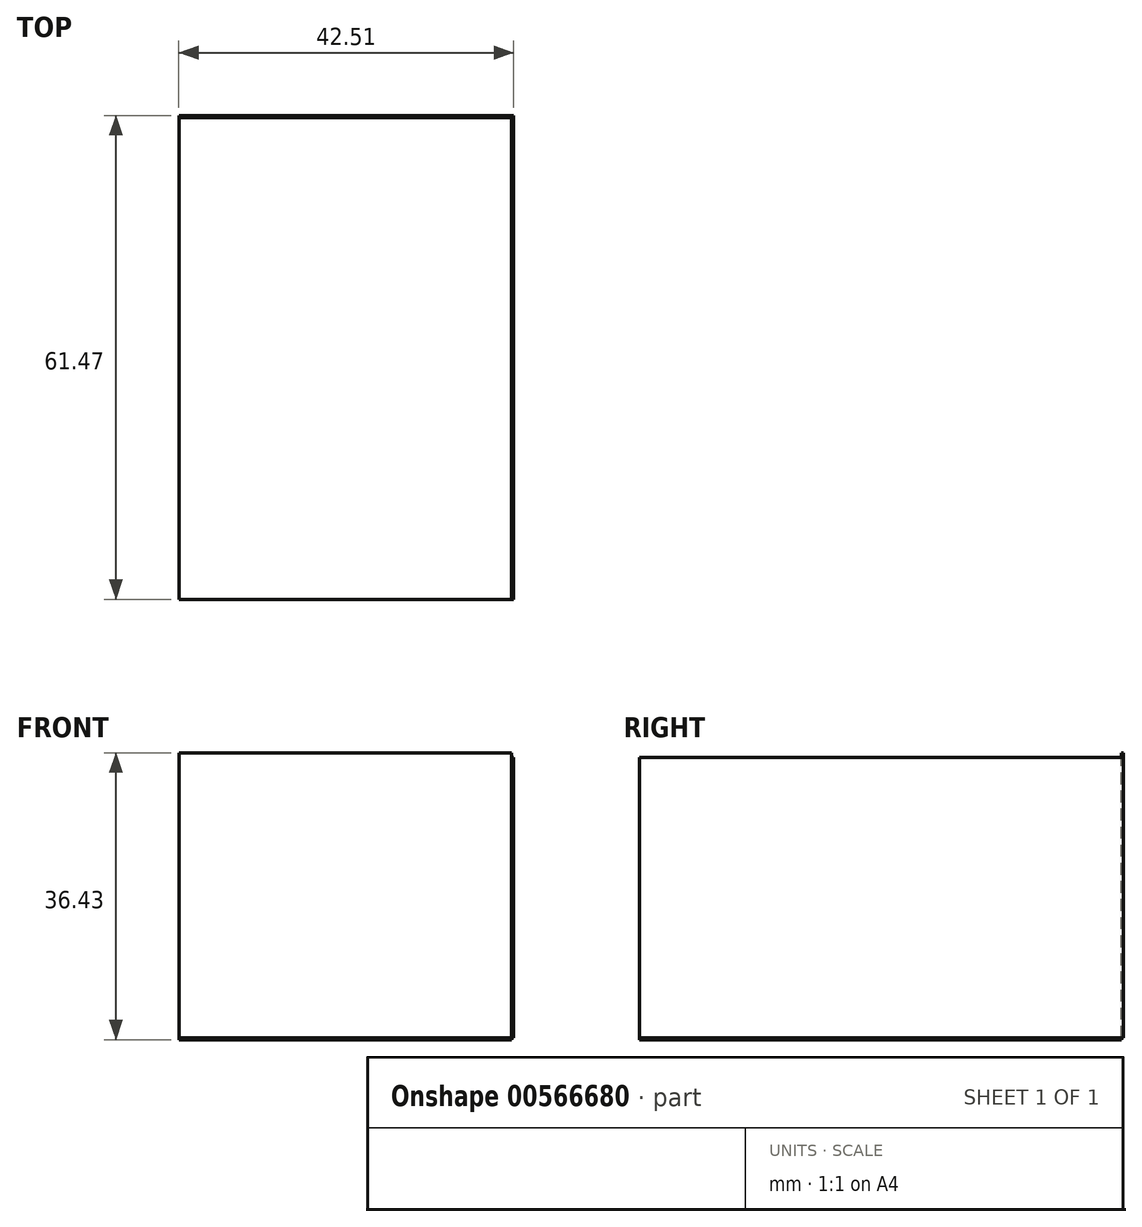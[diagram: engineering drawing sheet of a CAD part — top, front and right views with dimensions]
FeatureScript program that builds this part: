
annotation { "Feature Type Name" : "Feature", "Feature Type Description" : "" }
export const myFeature = defineFeature(function(context is Context, id is Id, definition is map)
    precondition{}
    {
        {
            var Q0;
            Q0=qCreatedBy(makeId("Top.planeOp"),FACE);
            var sketch = newSketch(context, id + "F0", { "sketchPlane" : qUnion([Q0])});
            skLineSegment(sketch, "E0.bottom", {"start": v(21.13, -30.6) * mm, "end": v(-21.13, -30.6) * mm});
            skLineSegment(sketch, "E0.top", {"start": v(21.13, 30.6) * mm, "end": v(-21.13, 30.6) * mm});
            skLineSegment(sketch, "E0.left", {"start": v(21.13, -30.6) * mm, "end": v(21.13, 30.6) * mm});
            skLineSegment(sketch, "E0.right", {"start": v(-21.13, -30.6) * mm, "end": v(-21.13, 30.6) * mm});
            skPoint(sketch, "E0.middle", {"position": v(0, 0) * mm});
            skSolve(sketch);
        }
        {
            var Q0;
            Q0 = qSketchRegion(id + "F0", true);
            extrude(context, id + "F1", {"entities" : qUnion([Q0]), "depth" : 0.25 * mm, "offsetDistance" : 25.4 * mm});
        }
        {
            var Q0;
            Q0=makeQuery(id+"F1.opExtrude","SWEPT_FACE",FACE,{"disambiguationData":[OSD([sQuery(id+"F0.wireOp",EDGE,"E0.top")])]});
            var sketch = newSketch(context, id + "F2", { "sketchPlane" : qUnion([Q0])});
            skLineSegment(sketch, "E1.bottom", {"start": v(-21.13, 0.25) * mm, "end": v(21.13, 0.25) * mm});
            skLineSegment(sketch, "E1.top", {"start": v(-21.13, 36.43) * mm, "end": v(21.13, 36.43) * mm});
            skLineSegment(sketch, "E1.left", {"start": v(-21.13, 0.25) * mm, "end": v(-21.13, 36.43) * mm});
            skLineSegment(sketch, "E1.right", {"start": v(21.13, 0.25) * mm, "end": v(21.13, 36.43) * mm});
            skSolve(sketch);
        }
        {
            var Q0;
            Q0=makeQuery(id+"F2.imprint","IMPRINT",FACE,{"disambiguationData":[TD([[makeQuery(id+"F2.imprint","IMPRINT",EDGE,{"derivedFrom":sQuery(id+"F2.wireOp",EDGE,"E1.bottom")}),1.0]])]});
            extrude(context, id + "F3", {"entities" : qUnion([Q0]), "depth" : 0.25 * mm, "offsetDistance" : 25.4 * mm});
        }
        {
            var Q0;
            Q0=makeQuery(id+"F1.opExtrude","SWEPT_FACE",FACE,{"disambiguationData":[OSD([sQuery(id+"F0.wireOp",EDGE,"E0.left")])]});
            var sketch = newSketch(context, id + "F4", { "sketchPlane" : qUnion([Q0])});
            skLineSegment(sketch, "E2.bottom", {"start": v(-30.6, 0.25) * mm, "end": v(30.84, 0.25) * mm});
            skLineSegment(sketch, "E2.top", {"start": v(-30.6, 35.83) * mm, "end": v(30.84, 35.83) * mm});
            skLineSegment(sketch, "E2.left", {"start": v(-30.6, 0.25) * mm, "end": v(-30.6, 35.83) * mm});
            skLineSegment(sketch, "E2.right", {"start": v(30.84, 0.25) * mm, "end": v(30.84, 35.83) * mm});
            skSolve(sketch);
        }
        {
            var Q0;
            Q0 = qSketchRegion(id + "F4", true);
            extrude(context, id + "F5", {"entities" : qUnion([Q0]), "operationType" : NewBodyOperationType.ADD, "depth" : 0.25 * mm, "offsetDistance" : 25.4 * mm});
        }
    });
